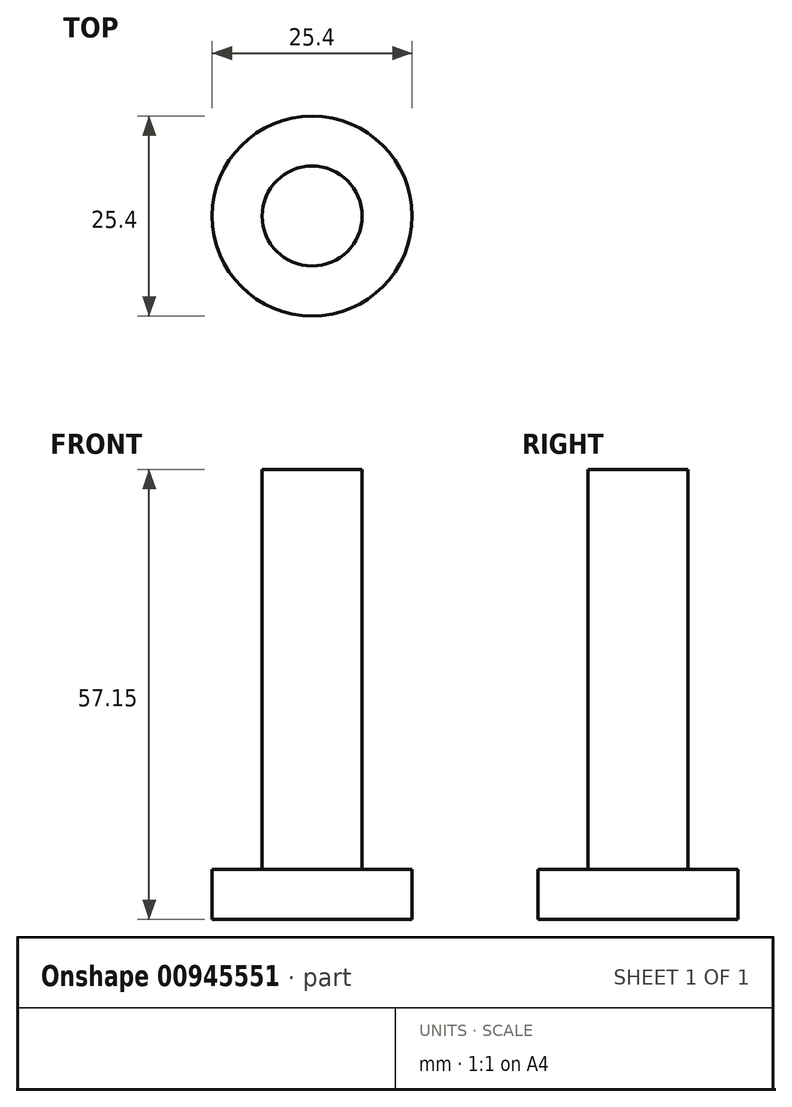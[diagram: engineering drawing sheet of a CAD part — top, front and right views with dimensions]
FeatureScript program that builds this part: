
annotation { "Feature Type Name" : "Feature", "Feature Type Description" : "" }
export const myFeature = defineFeature(function(context is Context, id is Id, definition is map)
    precondition{}
    {
        {
            var Q0;
            Q0=qCreatedBy(makeId("Top.planeOp"),FACE);
            var sketch = newSketch(context, id + "F0", { "sketchPlane" : qUnion([Q0])});
            skCircle(sketch, "E0", {"center": v(0, 0) * mm, "radius": 12.7 * mm});
            skSolve(sketch);
        }
        {
            var Q0;
            Q0=makeQuery(id+"F0.imprint","IMPRINT",FACE,{"disambiguationData":[TD([[makeQuery(id+"F0.imprint","IMPRINT",EDGE,{"derivedFrom":sQuery(id+"F0.wireOp",EDGE,"E0")}),1.0]])]});
            var sketch = newSketch(context, id + "F1", { "sketchPlane" : qUnion([Q0])});
            skCircle(sketch, "E1", {"center": v(0, 0) * mm, "radius": 6.35 * mm});
            skSolve(sketch);
        }
        {
            var Q0;
            Q0 = qSketchRegion(id + "F1", true);
            extrude(context, id + "F2", {"entities" : qUnion([Q0]), "depth" : 50.8 * mm, "offsetDistance" : 25.4 * mm});
        }
        {
            var Q0;
            Q0 = qSketchRegion(id + "F0", true);
            extrude(context, id + "F3", {"entities" : qUnion([Q0]), "operationType" : NewBodyOperationType.ADD, "oppositeDirection" : true, "depth" : 6.35 * mm, "offsetDistance" : 25.4 * mm});
        }
    });
